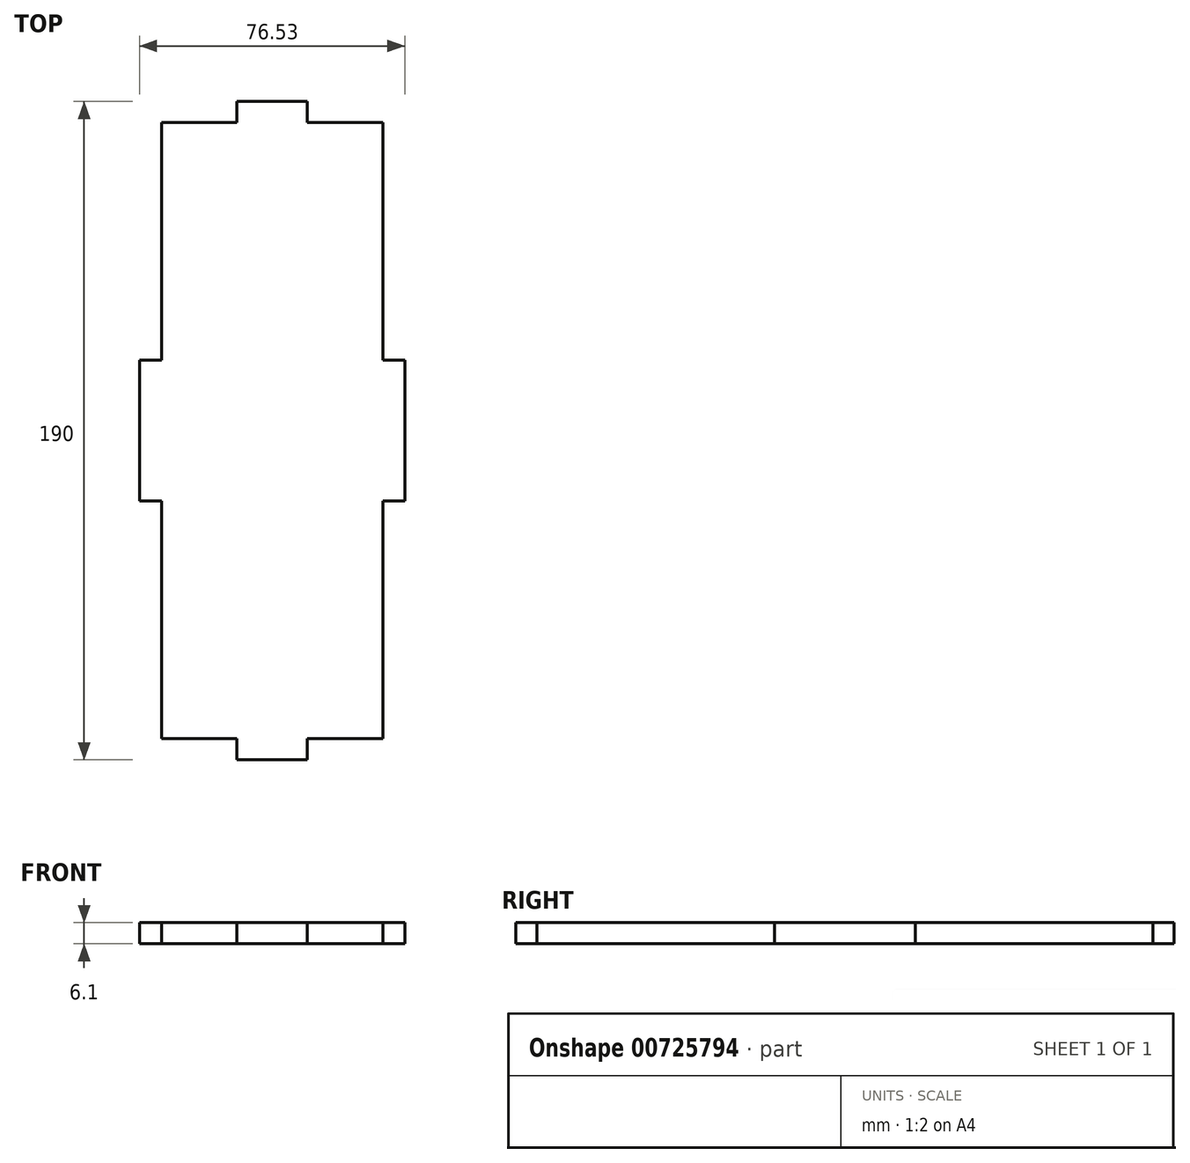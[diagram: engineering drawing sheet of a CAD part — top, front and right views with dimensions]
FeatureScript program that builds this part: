
annotation { "Feature Type Name" : "Feature", "Feature Type Description" : "" }
export const myFeature = defineFeature(function(context is Context, id is Id, definition is map)
    precondition{}
    {
        {
            var Q0;
            Q0=qCreatedBy(makeId("Top.planeOp"),FACE);
            var sketch = newSketch(context, id + "F0", { "sketchPlane" : qUnion([Q0])});
            skLineSegment(sketch, "E0.top", {"start": v(-6.35, 102.8) * mm, "end": v(0, 102.8) * mm});
            skLineSegment(sketch, "E1.MirrorCS", {"start": v(-6.35, 62.16) * mm, "end": v(0, 62.16) * mm});
            skLineSegment(sketch, "E2.MirrorCS", {"start": v(70.18, 102.8) * mm, "end": v(63.82, 102.8) * mm});
            skLineSegment(sketch, "E3.MirrorCS", {"start": v(70.18, 62.16) * mm, "end": v(63.83, 62.16) * mm});
            skLineSegment(sketch, "E4", {"start": v(-6.35, 62.16) * mm, "end": v(-6.35, 102.8) * mm});
            skLineSegment(sketch, "E5", {"start": v(70.18, 62.16) * mm, "end": v(70.18, 102.8) * mm});
            skLineSegment(sketch, "E6", {"start": v(0, 62.16) * mm, "end": v(0, -6.42) * mm});
            skLineSegment(sketch, "E7", {"start": v(63.83, 62.16) * mm, "end": v(63.83, -6.42) * mm});
            skLineSegment(sketch, "E8", {"start": v(0, 102.8) * mm, "end": v(0, 171.38) * mm});
            skLineSegment(sketch, "E9", {"start": v(63.82, 102.8) * mm, "end": v(63.82, 171.38) * mm});
            skLineSegment(sketch, "E10", {"start": v(0, -6.42) * mm, "end": v(21.75, -6.42) * mm});
            skLineSegment(sketch, "E11", {"start": v(63.82, 171.38) * mm, "end": v(42.07, 171.38) * mm});
            skLineSegment(sketch, "E12", {"start": v(63.83, -6.42) * mm, "end": v(42.07, -6.42) * mm});
            skLineSegment(sketch, "E13", {"start": v(42.07, -6.42) * mm, "end": v(42.07, -12.52) * mm});
            skLineSegment(sketch, "E14", {"start": v(42.07, -12.52) * mm, "end": v(21.75, -12.52) * mm});
            skLineSegment(sketch, "E15", {"start": v(21.75, -12.52) * mm, "end": v(21.75, -6.42) * mm});
            skPoint(sketch, "E16.orphan", {"position": v(31.91, -6.42) * mm});
            skLineSegment(sketch, "E17.MirrorCS", {"start": v(21.75, 177.48) * mm, "end": v(21.75, 171.38) * mm});
            skLineSegment(sketch, "E18.MirrorCS", {"start": v(42.07, 177.48) * mm, "end": v(21.75, 177.48) * mm});
            skLineSegment(sketch, "E19.MirrorCS", {"start": v(42.07, 171.38) * mm, "end": v(42.07, 177.48) * mm});
            skPoint(sketch, "E20.end.orphan", {"position": v(70.18, 82.48) * mm});
            skPoint(sketch, "E20.start.orphan", {"position": v(-6.35, 82.48) * mm});
            skLineSegment(sketch, "E21.trimOffspring", {"start": v(21.75, 171.38) * mm, "end": v(0, 171.38) * mm});
            skSolve(sketch);
        }
        {
            var Q0;
            Q0=makeQuery(id+"F0.imprint","IMPRINT",FACE,{"disambiguationData":[TD([[makeQuery(id+"F0.imprint","IMPRINT",EDGE,{"derivedFrom":sQuery(id+"F0.wireOp",EDGE,"E0.top")}),-1.0]])]});
            extrude(context, id + "F1", {"entities" : qUnion([Q0]), "depth" : 6.1 * mm, "offsetDistance" : 25.4 * mm});
        }
    });
